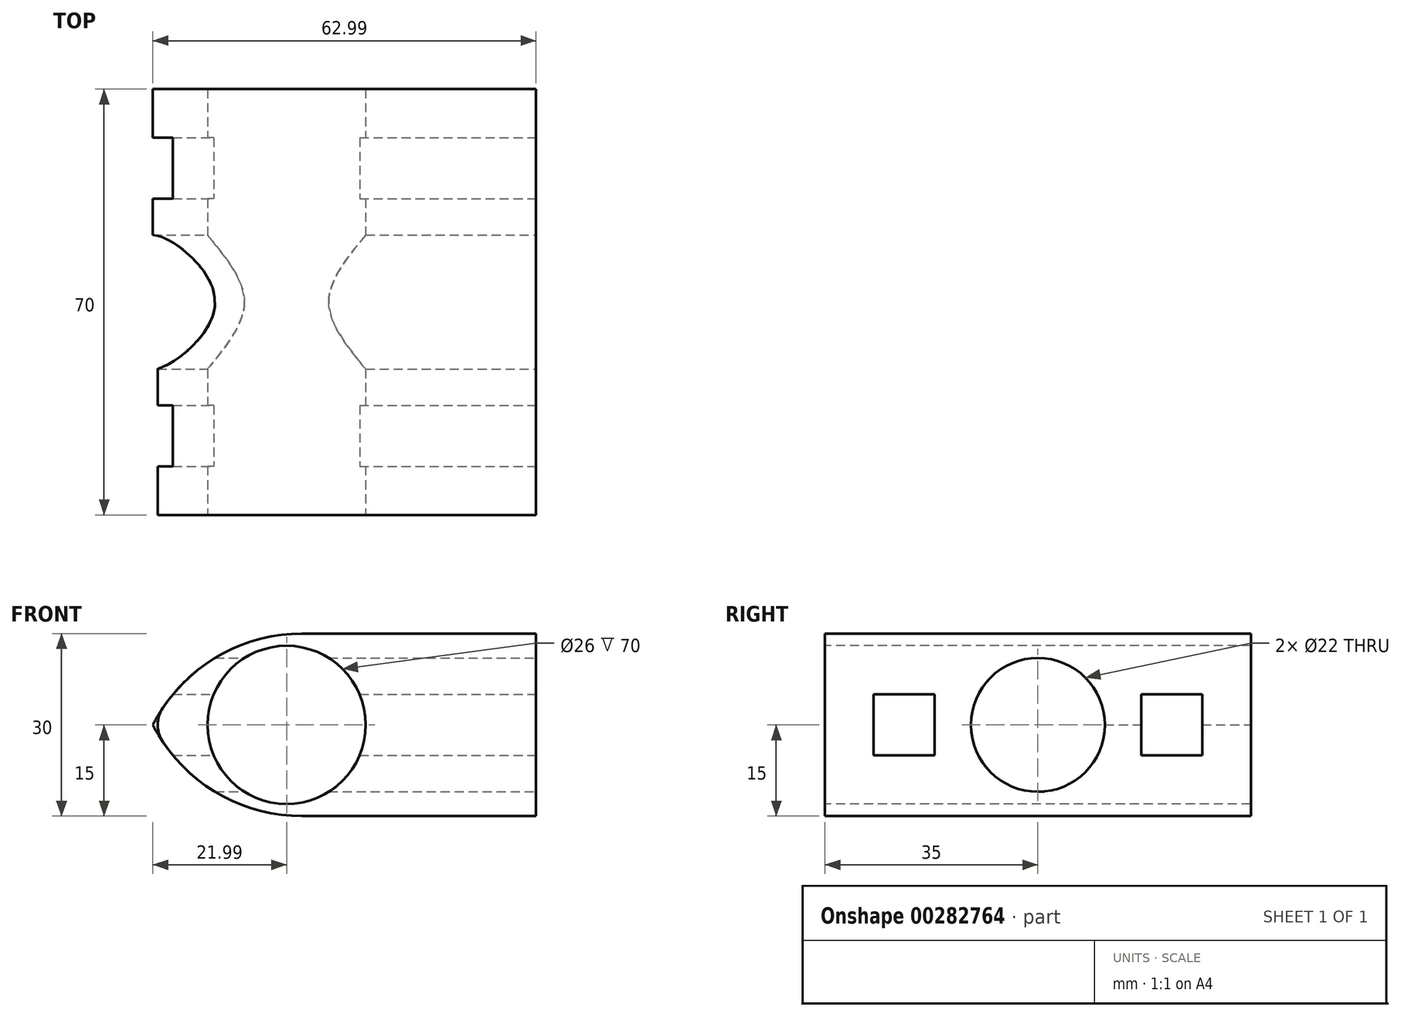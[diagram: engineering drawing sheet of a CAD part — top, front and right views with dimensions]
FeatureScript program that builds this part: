
annotation { "Feature Type Name" : "Feature", "Feature Type Description" : "" }
export const myFeature = defineFeature(function(context is Context, id is Id, definition is map)
    precondition{}
    {
        {
            var Q0;
            Q0=qCreatedBy(makeId("Right.planeOp"),FACE);
            var sketch = newSketch(context, id + "F0", { "sketchPlane" : qUnion([Q0])});
            skLineSegment(sketch, "E0.bottom", {"start": v(35, 15) * mm, "end": v(-35, 15) * mm});
            skLineSegment(sketch, "E0.top", {"start": v(35, -15) * mm, "end": v(-35, -15) * mm});
            skLineSegment(sketch, "E0.left", {"start": v(35, 15) * mm, "end": v(35, -15) * mm});
            skLineSegment(sketch, "E0.right", {"start": v(-35, 15) * mm, "end": v(-35, -15) * mm});
            skPoint(sketch, "E0.middle", {"position": v(0, 0) * mm});
            skSolve(sketch);
        }
        {
            var Q0;
            Q0=makeQuery(id+"F0.imprint","IMPRINT",FACE,{"disambiguationData":[TD([[makeQuery(id+"F0.imprint","IMPRINT",EDGE,{"derivedFrom":sQuery(id+"F0.wireOp",EDGE,"E0.bottom")}),1.0]])]});
            extrude(context, id + "F1", {"entities" : qUnion([Q0]), "oppositeDirection" : true, "depth" : 66 * mm});
        }
        {
            var Q0;
            Q0=makeQuery(id+"F1.opExtrude","SWEPT_FACE",FACE,{"disambiguationData":[OSD([sQuery(id+"F0.wireOp",EDGE,"E0.right")])]});
            var sketch = newSketch(context, id + "F2", { "sketchPlane" : qUnion([Q0])});
            skLineSegment(sketch, "E1", {"start": v(0, 0) * mm, "end": v(-16, 0) * mm});
            skLineSegment(sketch, "E2", {"start": v(-16, 15) * mm, "end": v(-16, -15) * mm});
            skLineSegment(sketch, "E3", {"start": v(-16, -15) * mm, "end": v(-16, 15) * mm});
            skLineSegment(sketch, "E4", {"start": v(-16, 15) * mm, "end": v(-66, 15) * mm});
            skLineSegment(sketch, "E5", {"start": v(-66, 15) * mm, "end": v(-16, 15) * mm});
            skLineSegment(sketch, "E6", {"start": v(-41, 15) * mm, "end": v(-41, 0) * mm});
            skCircle(sketch, "E7", {"center": v(-41, 0) * mm, "radius": 25 * mm});
            skSolve(sketch);
        }
        {
            var Q0;
            {var subQ0=sQuery(id+"F2.wireOp",EDGE,"E5");var subQ1=makeQuery(id+"F2.imprint","IMPRINT",VERTEX,{"derivedFrom":subQ0});Q0=makeQuery(id+"F2.imprint","IMPRINT",FACE,{"disambiguationData":[TD([[makeQuery(id+"F2.imprint","IMPRINT",EDGE,{"disambiguationData":[TD([[subQ1,1.0]])],"derivedFrom":subQ0}),1.0]])]});}
            var Q1;
            {var subQ2=sQuery(id+"F2.wireOp",EDGE,"E5");var subQ4=makeQuery(id+"F2.imprint","IMPRINT",VERTEX,{"derivedFrom":subQ2});Q1=makeQuery(id+"F2.imprint","IMPRINT",FACE,{"disambiguationData":[TD([[makeQuery(id+"F2.imprint","IMPRINT",EDGE,{"disambiguationData":[TD([[subQ4,1.0]])],"derivedFrom":subQ2}),-1.0]])]});}
            var Q2;
            {var subQ0=sQuery(id+"F2.wireOp",EDGE,"E7");var subQ1=makeQuery(id+"F1.opExtrude","SWEPT_EDGE",EDGE,{"disambiguationData":[OSD([sQuery(id+"F0.wireOp",EDGE,"E0.top"),sQuery(id+"F0.wireOp",EDGE,"E0.right")])]});var subQ2=makeQuery(id+"F2.imprint","INTERSECT",VERTEX,{"disambiguationData":[OD(0.0)],"derivedFrom":[subQ1,subQ0]});Q2=makeQuery(id+"F2.imprint","IMPRINT",FACE,{"disambiguationData":[TD([[makeQuery(id+"F2.imprint","IMPRINT",EDGE,{"disambiguationData":[TD([[subQ2,-1.0]])],"derivedFrom":subQ0}),1.0]])]});}
            extrude(context, id + "F3", {"entities" : qUnion([Q0, Q1, Q2]), "operationType" : NewBodyOperationType.ADD, "oppositeDirection" : true, "depth" : 70 * mm});
        }
        {
            var Q0;
            Q0=makeQuery(id+"F3.boolean.opBoolean","MERGE",FACE,{"derivedFrom":[makeQuery(id+"F1.opExtrude","SWEPT_FACE",FACE,{"disambiguationData":[OSD([sQuery(id+"F0.wireOp",EDGE,"E0.right")])]}),makeQuery(id+"F3.opExtrude","CAP_FACE",FACE,{"disambiguationData":[OSD([sQuery(id+"F2.wireOp",EDGE,"E7")])],"isStart":true})]});
            var sketch = newSketch(context, id + "F4", { "sketchPlane" : qUnion([Q0])});
            skCircle(sketch, "E8", {"center": v(-41, 0) * mm, "radius": 13 * mm});
            skSolve(sketch);
        }
        {
            var Q0;
            Q0=makeQuery(id+"F4.imprint","IMPRINT",FACE,{"disambiguationData":[TD([[makeQuery(id+"F4.imprint","IMPRINT",EDGE,{"derivedFrom":sQuery(id+"F4.wireOp",EDGE,"E8")}),1.0]])]});
            extrude(context, id + "F5", {"entities" : qUnion([Q0]), "operationType" : NewBodyOperationType.REMOVE, "oppositeDirection" : true, "depth" : 71 * mm});
        }
        {
            var Q0;
            Q0=makeQuery(id+"F1.opExtrude","CAP_FACE",FACE,{"disambiguationData":[OSD([sQuery(id+"F0.wireOp",EDGE,"E0.bottom"),sQuery(id+"F0.wireOp",EDGE,"E0.top"),sQuery(id+"F0.wireOp",EDGE,"E0.left"),sQuery(id+"F0.wireOp",EDGE,"E0.right")])],"isStart":true});
            var sketch = newSketch(context, id + "F6", { "sketchPlane" : qUnion([Q0])});
            skLineSegment(sketch, "E9", {"start": v(35, 15) * mm, "end": v(35, 5) * mm});
            skLineSegment(sketch, "E10", {"start": v(35, 5) * mm, "end": v(35, -5) * mm});
            skLineSegment(sketch, "E11", {"start": v(-35, 15) * mm, "end": v(-27, 15) * mm});
            skLineSegment(sketch, "E12", {"start": v(-27, 15) * mm, "end": v(-17, 15) * mm});
            skLineSegment(sketch, "E13", {"start": v(-17, 15) * mm, "end": v(-17, 5) * mm});
            skLineSegment(sketch, "E14", {"start": v(-17, 5) * mm, "end": v(-27, 5) * mm});
            skLineSegment(sketch, "E15", {"start": v(-27, 5) * mm, "end": v(-27, -5) * mm});
            skLineSegment(sketch, "E16", {"start": v(-27, -5) * mm, "end": v(-17, -5) * mm});
            skLineSegment(sketch, "E17", {"start": v(-17, -5) * mm, "end": v(-17, 5) * mm});
            skLineSegment(sketch, "E18", {"start": v(35, 15) * mm, "end": v(27, 15) * mm});
            skLineSegment(sketch, "E19", {"start": v(27, 15) * mm, "end": v(17, 15) * mm});
            skLineSegment(sketch, "E20", {"start": v(17, 15) * mm, "end": v(17, 5) * mm});
            skLineSegment(sketch, "E21", {"start": v(17, 5) * mm, "end": v(27, 5) * mm});
            skLineSegment(sketch, "E22", {"start": v(27, 5) * mm, "end": v(27, -5) * mm});
            skLineSegment(sketch, "E23", {"start": v(27, -5) * mm, "end": v(17, -5) * mm});
            skLineSegment(sketch, "E24", {"start": v(17, -5) * mm, "end": v(17, 5) * mm});
            skCircle(sketch, "E25", {"center": v(0, 0) * mm, "radius": 11 * mm});
            skSolve(sketch);
        }
        {
            var Q0;
            Q0=makeQuery(id+"F6.imprint","IMPRINT",FACE,{"disambiguationData":[TD([[makeQuery(id+"F6.imprint","IMPRINT",EDGE,{"derivedFrom":sQuery(id+"F6.wireOp",EDGE,"E14")}),1.0]])]});
            var Q1;
            Q1=makeQuery(id+"F6.imprint","IMPRINT",FACE,{"disambiguationData":[TD([[makeQuery(id+"F6.imprint","IMPRINT",EDGE,{"derivedFrom":sQuery(id+"F6.wireOp",EDGE,"E25")}),1.0]])]});
            var Q2;
            Q2=makeQuery(id+"F6.imprint","IMPRINT",FACE,{"disambiguationData":[TD([[makeQuery(id+"F6.imprint","IMPRINT",EDGE,{"derivedFrom":sQuery(id+"F6.wireOp",EDGE,"E21")}),-1.0]])]});
            extrude(context, id + "F7", {"entities" : qUnion([Q0, Q1, Q2]), "operationType" : NewBodyOperationType.REMOVE, "oppositeDirection" : true, "depth" : 70 * mm});
        }
        {
            var Q0;
            Q0=makeQuery(id+"F1.opExtrude","CAP_EDGE",EDGE,{"disambiguationData":[OSD([sQuery(id+"F0.wireOp",EDGE,"E0.bottom")])],"isStart":false});
            var Q1;
            Q1=makeQuery(id+"F1.opExtrude","CAP_EDGE",EDGE,{"disambiguationData":[OSD([sQuery(id+"F0.wireOp",EDGE,"E0.top")])],"isStart":false});
            fillet(context, id + "F8", {"entities" : qUnion([Q0, Q1]), "radius" : 27.52 * mm, "tangentPropagation" : true, "allowEdgeOverflow" : false});
        }
        {
            var Q0;
            Q0=makeQuery(id+"F8.opFillet","BLEND_EDGE",EDGE,{"disambiguationData":[OD(1.0)],"blendedFrom":[makeQuery(id+"F1.opExtrude","CAP_EDGE",EDGE,{"disambiguationData":[OSD([sQuery(id+"F0.wireOp",EDGE,"E0.bottom")])],"isStart":false}),makeQuery(id+"F1.opExtrude","CAP_EDGE",EDGE,{"disambiguationData":[OSD([sQuery(id+"F0.wireOp",EDGE,"E0.top")])],"isStart":false})],"blendedInto":[]});
            var Q1;
            Q1=makeQuery(id+"F8.opFillet","BLEND_EDGE",EDGE,{"disambiguationData":[OD(2.0)],"blendedFrom":[makeQuery(id+"F1.opExtrude","CAP_EDGE",EDGE,{"disambiguationData":[OSD([sQuery(id+"F0.wireOp",EDGE,"E0.bottom")])],"isStart":false}),makeQuery(id+"F1.opExtrude","CAP_EDGE",EDGE,{"disambiguationData":[OSD([sQuery(id+"F0.wireOp",EDGE,"E0.top")])],"isStart":false})],"blendedInto":[]});
            fillet(context, id + "F9", {"entities" : qUnion([Q0, Q1]), "radius" : 5 * mm, "tangentPropagation" : true, "allowEdgeOverflow" : false});
        }
    });
